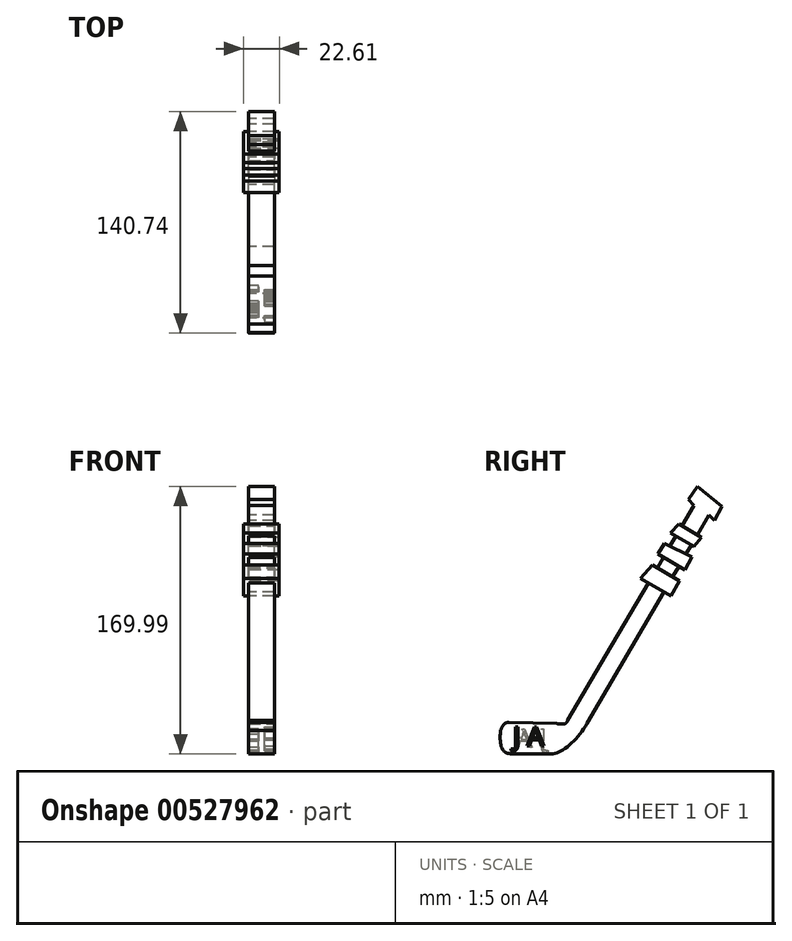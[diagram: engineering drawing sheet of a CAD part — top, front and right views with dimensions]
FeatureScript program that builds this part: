
annotation { "Feature Type Name" : "Feature", "Feature Type Description" : "" }
export const myFeature = defineFeature(function(context is Context, id is Id, definition is map)
    precondition{}
    {
        {
            var Q0;
            Q0=qCreatedBy(makeId("Right.planeOp"),FACE);
            var sketch = newSketch(context, id + "F0", { "sketchPlane" : qUnion([Q0])});
            skFitSpline(sketch, "E0", {"points": [v(0, 0) * mm, v(-16.58, -17.53) * mm, v(-30.01, -19.37) * mm], "startDerivative": vector(-21.4, -38.91) * mm, "endDerivative": vector(-38.92, 0.78) * mm});
            skLineSegment(sketch, "E1", {"start": v(-30.01, -19.37) * mm, "end": v(-45.64, -19.37) * mm});
            skFitSpline(sketch, "E2", {"points": [v(-45.64, -19.37) * mm, v(-53.94, -15.79) * mm, v(-54.85, -4.38) * mm, v(-54.85, -4.38) * mm], "startDerivative": vector(-22.65, 1.57) * mm, "endDerivative": vector(-0.12, 0.82) * mm});
            skFitSpline(sketch, "E3", {"points": [v(-54.85, -4.38) * mm, v(-52.18, 0) * mm, v(-49.35, 0.87) * mm], "startDerivative": vector(4.2, 9.27) * mm, "endDerivative": vector(6.95, 0.8) * mm});
            skLineSegment(sketch, "E4", {"start": v(-49.35, 0.87) * mm, "end": v(-18.89, 0) * mm});
            skFitSpline(sketch, "E5", {"points": [v(-18.89, 0) * mm, v(-13.68, 0) * mm, v(-12.19, 1.86) * mm, v(-11.32, 4.31) * mm], "startDerivative": vector(12.33, -3.5) * mm, "endDerivative": vector(-4.35, 0.33) * mm});
            skLineSegment(sketch, "E6", {"start": v(0, 0) * mm, "end": v(24.37, 41.62) * mm});
            skLineSegment(sketch, "E7", {"start": v(-12.19, 1.86) * mm, "end": v(12.19, 43.48) * mm});
            skPoint(sketch, "E7.endSnap0", {"position": v(12.19, 20.8) * mm});
            skLineSegment(sketch, "E8", {"start": v(12.19, 43.48) * mm, "end": v(37.33, 86.24) * mm});
            skLineSegment(sketch, "E9", {"start": v(24.37, 41.62) * mm, "end": v(50.5, 86.24) * mm});
            skLineSegment(sketch, "E10", {"start": v(37.33, 86.24) * mm, "end": v(68.12, 138.6) * mm});
            skLineSegment(sketch, "E11", {"start": v(50.5, 86.24) * mm, "end": v(77.56, 132.44) * mm});
            skLineSegment(sketch, "E12", {"start": v(77.56, 132.44) * mm, "end": v(81.23, 128.92) * mm});
            skLineSegment(sketch, "E13", {"start": v(68.12, 138.6) * mm, "end": v(64.66, 142.32) * mm});
            skLineSegment(sketch, "E14", {"start": v(64.66, 142.32) * mm, "end": v(70.25, 150.56) * mm});
            skLineSegment(sketch, "E15", {"start": v(81.23, 128.92) * mm, "end": v(85.72, 137.8) * mm});
            skLineSegment(sketch, "E16", {"start": v(70.25, 150.56) * mm, "end": v(85.72, 137.8) * mm});
            skSolve(sketch);
        }
        {
            var Q0;
            Q0=makeQuery(id+"F0.imprint","IMPRINT",FACE,{"disambiguationData":[TD([[makeQuery(id+"F0.imprint","IMPRINT",EDGE,{"derivedFrom":sQuery(id+"F0.wireOp",EDGE,"E0")}),-1.0]])]});
            extrude(context, id + "F1", {"entities" : qUnion([Q0]), "depth" : 16.5 * mm, "offsetDistance" : 25.4 * mm});
        }
        {
            var Q0;
            Q0=makeQuery(id+"F1.opExtrude","CAP_FACE",FACE,{"disambiguationData":[OSD([sQuery(id+"F0.wireOp",EDGE,"E0"),sQuery(id+"F0.wireOp",EDGE,"E1"),sQuery(id+"F0.wireOp",EDGE,"E2"),sQuery(id+"F0.wireOp",EDGE,"E3"),sQuery(id+"F0.wireOp",EDGE,"E4"),sQuery(id+"F0.wireOp",EDGE,"E5"),sQuery(id+"F0.wireOp",EDGE,"E6"),sQuery(id+"F0.wireOp",EDGE,"E7"),sQuery(id+"F0.wireOp",EDGE,"E8"),sQuery(id+"F0.wireOp",EDGE,"E9"),sQuery(id+"F0.wireOp",EDGE,"E10"),sQuery(id+"F0.wireOp",EDGE,"E11"),sQuery(id+"F0.wireOp",EDGE,"E12"),sQuery(id+"F0.wireOp",EDGE,"E13"),sQuery(id+"F0.wireOp",EDGE,"E14"),sQuery(id+"F0.wireOp",EDGE,"E15"),sQuery(id+"F0.wireOp",EDGE,"E16")])],"isStart":false});
            var sketch = newSketch(context, id + "F2", { "sketchPlane" : qUnion([Q0])});
            skLineSegment(sketch, "E17", {"start": v(58.5, 126.73) * mm, "end": v(72.93, 118.24) * mm});
            skLineSegment(sketch, "E18", {"start": v(72.93, 118.24) * mm, "end": v(68.12, 112.37) * mm});
            skLineSegment(sketch, "E19", {"start": v(68.12, 112.37) * mm, "end": v(53.12, 121.19) * mm});
            skLineSegment(sketch, "E20", {"start": v(53.12, 121.19) * mm, "end": v(58.5, 126.73) * mm});
            skSolve(sketch);
        }
        {
            var Q0;
            {var subQ0=sQuery(id+"F2.wireOp",EDGE,"E20");Q0=makeQuery(id+"F2.imprint","IMPRINT",FACE,{"disambiguationData":[TD([[makeQuery(id+"F2.imprint","IMPRINT",EDGE,{"derivedFrom":subQ0}),-1.0]])]});}
            var Q1;
            {var subQ0=sQuery(id+"F2.wireOp",EDGE,"E17");var subQ1=makeQuery(id+"F1.opExtrude","CAP_EDGE",EDGE,{"disambiguationData":[OSD([sQuery(id+"F0.wireOp",EDGE,"E8"),sQuery(id+"F0.wireOp",EDGE,"E10")])],"isStart":false});var subQ2=makeQuery(id+"F2.imprint","INTERSECT",VERTEX,{"derivedFrom":[subQ1,subQ0]});Q1=makeQuery(id+"F2.imprint","IMPRINT",FACE,{"disambiguationData":[TD([[makeQuery(id+"F2.imprint","IMPRINT",EDGE,{"disambiguationData":[TD([[subQ2,-1.0]])],"derivedFrom":subQ0}),-1.0]])]});}
            var Q2;
            {var subQ0=sQuery(id+"F2.wireOp",EDGE,"E18");Q2=makeQuery(id+"F2.imprint","IMPRINT",FACE,{"disambiguationData":[TD([[makeQuery(id+"F2.imprint","IMPRINT",EDGE,{"derivedFrom":subQ0}),-1.0]])]});}
            extrude(context, id + "F3", {"entities" : qUnion([Q0, Q1, Q2]), "operationType" : NewBodyOperationType.ADD, "depth" : 3.05 * mm, "offsetDistance" : 25.4 * mm});
        }
        {
            var Q0;
            Q0 = qSketchRegion(id + "F2", true);
            extrude(context, id + "F4", {"entities" : qUnion([Q0]), "operationType" : NewBodyOperationType.ADD, "oppositeDirection" : true, "depth" : 19.56 * mm, "offsetDistance" : 25.4 * mm});
        }
        {
            var Q0;
            {var subQ1=sQuery(id+"F0.wireOp",EDGE,"E3");var subQ2=sQuery(id+"F0.wireOp",EDGE,"E10");var subQ3=sQuery(id+"F0.wireOp",EDGE,"E8");var subQ4=sQuery(id+"F0.wireOp",EDGE,"E7");var subQ5=sQuery(id+"F0.wireOp",EDGE,"E11");var subQ6=sQuery(id+"F0.wireOp",EDGE,"E9");var subQ7=sQuery(id+"F0.wireOp",EDGE,"E6");var subQ8=sQuery(id+"F0.wireOp",EDGE,"E5");var subQ9=sQuery(id+"F0.wireOp",EDGE,"E4");var subQ10=sQuery(id+"F0.wireOp",EDGE,"E0");var subQ11=sQuery(id+"F0.wireOp",EDGE,"E1");var subQ12=sQuery(id+"F0.wireOp",EDGE,"E2");Q0=makeQuery(id+"F3.boolean.opBoolean","SPLIT",FACE,{"disambiguationData":[TD([makeQuery(id+"F1.opExtrude","SWEPT_FACE",FACE,{"disambiguationData":[OSD([subQ10])]})])],"derivedFrom":makeQuery(id+"F1.opExtrude","CAP_FACE",FACE,{"disambiguationData":[OSD([subQ10,subQ11,subQ12,subQ1,subQ9,subQ8,subQ7,subQ4,subQ3,subQ6,subQ2,subQ5,sQuery(id+"F0.wireOp",EDGE,"E12"),sQuery(id+"F0.wireOp",EDGE,"E13"),sQuery(id+"F0.wireOp",EDGE,"E14"),sQuery(id+"F0.wireOp",EDGE,"E15"),sQuery(id+"F0.wireOp",EDGE,"E16")])],"isStart":false})});}
            var sketch = newSketch(context, id + "F5", { "sketchPlane" : qUnion([Q0])});
            skLineSegment(sketch, "E21", {"start": v(49.34, 114.45) * mm, "end": v(45.32, 107.6) * mm});
            skLineSegment(sketch, "E22", {"start": v(45.32, 107.6) * mm, "end": v(62.17, 97.7) * mm});
            skLineSegment(sketch, "E23", {"start": v(62.17, 97.7) * mm, "end": v(66.91, 105.76) * mm});
            skLineSegment(sketch, "E24", {"start": v(66.91, 105.76) * mm, "end": v(49.34, 114.45) * mm});
            skSolve(sketch);
        }
        {
            var Q0;
            Q0 = qSketchRegion(id + "F5", true);
            extrude(context, id + "F6", {"entities" : qUnion([Q0]), "operationType" : NewBodyOperationType.ADD, "depth" : 3.05 * mm, "offsetDistance" : 25.4 * mm});
        }
        {
            var Q0;
            Q0 = qSketchRegion(id + "F5", true);
            extrude(context, id + "F7", {"entities" : qUnion([Q0]), "operationType" : NewBodyOperationType.ADD, "oppositeDirection" : true, "depth" : 19.56 * mm, "offsetDistance" : 25.4 * mm});
        }
        {
            var Q0;
            {var subQ0=sQuery(id+"F0.wireOp",EDGE,"E10");var subQ1=sQuery(id+"F0.wireOp",EDGE,"E8");var subQ3=sQuery(id+"F0.wireOp",EDGE,"E7");var subQ5=sQuery(id+"F0.wireOp",EDGE,"E11");var subQ6=sQuery(id+"F0.wireOp",EDGE,"E9");var subQ7=sQuery(id+"F0.wireOp",EDGE,"E6");var subQ9=sQuery(id+"F0.wireOp",EDGE,"E5");var subQ11=sQuery(id+"F0.wireOp",EDGE,"E4");var subQ13=sQuery(id+"F0.wireOp",EDGE,"E0");var subQ14=makeQuery(id+"F1.opExtrude","SWEPT_FACE",FACE,{"disambiguationData":[OSD([subQ13])]});var subQ15=sQuery(id+"F0.wireOp",EDGE,"E3");var subQ17=sQuery(id+"F0.wireOp",EDGE,"E1");var subQ20=sQuery(id+"F0.wireOp",EDGE,"E2");Q0=makeQuery(id+"F6.boolean.opBoolean","SPLIT",FACE,{"disambiguationData":[TD([subQ14])],"derivedFrom":makeQuery(id+"F3.boolean.opBoolean","SPLIT",FACE,{"disambiguationData":[TD([subQ14])],"derivedFrom":makeQuery(id+"F1.opExtrude","CAP_FACE",FACE,{"disambiguationData":[OSD([subQ13,subQ17,subQ20,subQ15,subQ11,subQ9,subQ7,subQ3,subQ1,subQ6,subQ0,subQ5,sQuery(id+"F0.wireOp",EDGE,"E12"),sQuery(id+"F0.wireOp",EDGE,"E13"),sQuery(id+"F0.wireOp",EDGE,"E14"),sQuery(id+"F0.wireOp",EDGE,"E15"),sQuery(id+"F0.wireOp",EDGE,"E16")])],"isStart":false})})});}
            var sketch = newSketch(context, id + "F8", { "sketchPlane" : qUnion([Q0])});
            skLineSegment(sketch, "E25", {"start": v(41.6, 100.64) * mm, "end": v(58.94, 90.44) * mm});
            skLineSegment(sketch, "E26", {"start": v(58.94, 90.44) * mm, "end": v(53.35, 80.94) * mm});
            skLineSegment(sketch, "E27", {"start": v(53.35, 80.94) * mm, "end": v(34.14, 92.24) * mm});
            skLineSegment(sketch, "E28", {"start": v(34.14, 92.24) * mm, "end": v(41.6, 100.64) * mm});
            skSolve(sketch);
        }
        {
            var Q0;
            Q0 = qSketchRegion(id + "F8", true);
            extrude(context, id + "F9", {"entities" : qUnion([Q0]), "operationType" : NewBodyOperationType.ADD, "depth" : 3.05 * mm, "offsetDistance" : 25.4 * mm});
        }
        {
            var Q0;
            Q0 = qSketchRegion(id + "F8", true);
            extrude(context, id + "F10", {"entities" : qUnion([Q0]), "operationType" : NewBodyOperationType.ADD, "oppositeDirection" : true, "depth" : 19.56 * mm, "offsetDistance" : 25.4 * mm});
        }
        {
            var Q0;
            {var subQ0=sQuery(id+"F0.wireOp",EDGE,"E10");var subQ1=sQuery(id+"F0.wireOp",EDGE,"E8");var subQ3=sQuery(id+"F0.wireOp",EDGE,"E7");var subQ5=sQuery(id+"F0.wireOp",EDGE,"E11");var subQ6=sQuery(id+"F0.wireOp",EDGE,"E9");var subQ7=sQuery(id+"F0.wireOp",EDGE,"E6");var subQ9=sQuery(id+"F0.wireOp",EDGE,"E5");var subQ12=sQuery(id+"F0.wireOp",EDGE,"E4");var subQ14=sQuery(id+"F0.wireOp",EDGE,"E0");var subQ15=makeQuery(id+"F1.opExtrude","SWEPT_FACE",FACE,{"disambiguationData":[OSD([subQ14])]});var subQ16=sQuery(id+"F0.wireOp",EDGE,"E3");var subQ18=sQuery(id+"F0.wireOp",EDGE,"E1");var subQ20=sQuery(id+"F0.wireOp",EDGE,"E2");Q0=makeQuery(id+"F9.boolean.opBoolean","SPLIT",FACE,{"disambiguationData":[TD([subQ15])],"derivedFrom":makeQuery(id+"F6.boolean.opBoolean","SPLIT",FACE,{"disambiguationData":[TD([subQ15])],"derivedFrom":makeQuery(id+"F3.boolean.opBoolean","SPLIT",FACE,{"disambiguationData":[TD([subQ15])],"derivedFrom":makeQuery(id+"F1.opExtrude","CAP_FACE",FACE,{"disambiguationData":[OSD([subQ14,subQ18,subQ20,subQ16,subQ12,subQ9,subQ7,subQ3,subQ1,subQ6,subQ0,subQ5,sQuery(id+"F0.wireOp",EDGE,"E12"),sQuery(id+"F0.wireOp",EDGE,"E13"),sQuery(id+"F0.wireOp",EDGE,"E14"),sQuery(id+"F0.wireOp",EDGE,"E15"),sQuery(id+"F0.wireOp",EDGE,"E16")])],"isStart":false})})})});}
            var sketch = newSketch(context, id + "F11", { "sketchPlane" : qUnion([Q0])});
            skText(sketch, "E29", { "text": "J A", "fontName": "OpenSans-Regular.ttf"});
            const initialGuessF11  = {"E29": [-0.0468, -0.01422, 1, 0, 0.01214]};
            skSetInitialGuess(sketch, initialGuessF11);
            skSolve(sketch);
        }
        {
            var Q0;
            Q0 = qSketchRegion(id + "F11", true);
            extrude(context, id + "F12", {"entities" : qUnion([Q0]), "operationType" : NewBodyOperationType.REMOVE, "oppositeDirection" : true, "depth" : 12.7 * mm, "offsetDistance" : 25.4 * mm, "symmetric" : true});
        }
        {
            var Q0;
            {var subQ0=sQuery(id+"F0.wireOp",EDGE,"E10");var subQ1=sQuery(id+"F0.wireOp",EDGE,"E8");var subQ4=sQuery(id+"F0.wireOp",EDGE,"E7");var subQ6=sQuery(id+"F0.wireOp",EDGE,"E11");var subQ7=sQuery(id+"F0.wireOp",EDGE,"E9");var subQ8=sQuery(id+"F0.wireOp",EDGE,"E6");var subQ10=sQuery(id+"F0.wireOp",EDGE,"E5");var subQ12=sQuery(id+"F0.wireOp",EDGE,"E4");var subQ14=sQuery(id+"F0.wireOp",EDGE,"E0");var subQ15=makeQuery(id+"F1.opExtrude","SWEPT_FACE",FACE,{"disambiguationData":[OSD([subQ14])]});var subQ16=sQuery(id+"F0.wireOp",EDGE,"E3");var subQ18=sQuery(id+"F0.wireOp",EDGE,"E1");var subQ20=sQuery(id+"F0.wireOp",EDGE,"E2");Q0=makeQuery(id+"F10.boolean.opBoolean","SPLIT",FACE,{"disambiguationData":[TD([subQ15])],"derivedFrom":makeQuery(id+"F7.boolean.opBoolean","SPLIT",FACE,{"disambiguationData":[TD([subQ15])],"derivedFrom":makeQuery(id+"F4.boolean.opBoolean","SPLIT",FACE,{"disambiguationData":[TD([subQ15])],"derivedFrom":makeQuery(id+"F1.opExtrude","CAP_FACE",FACE,{"disambiguationData":[OSD([subQ14,subQ18,subQ20,subQ16,subQ12,subQ10,subQ8,subQ4,subQ1,subQ7,subQ0,subQ6,sQuery(id+"F0.wireOp",EDGE,"E12"),sQuery(id+"F0.wireOp",EDGE,"E13"),sQuery(id+"F0.wireOp",EDGE,"E14"),sQuery(id+"F0.wireOp",EDGE,"E15"),sQuery(id+"F0.wireOp",EDGE,"E16")])],"isStart":true})})})});}
            var sketch = newSketch(context, id + "F13", { "sketchPlane" : qUnion([Q0])});
            skText(sketch, "E30", { "text": "J A", "fontName": "OpenSans-Regular.ttf"});
            const initialGuessF13  = {"E30": [0.02604, -0.0152, 1, 0, 0.01192]};
            skSetInitialGuess(sketch, initialGuessF13);
            skSolve(sketch);
        }
        {
            var Q0;
            Q0 = qSketchRegion(id + "F13", true);
            extrude(context, id + "F14", {"entities" : qUnion([Q0]), "operationType" : NewBodyOperationType.REMOVE, "oppositeDirection" : true, "depth" : 12.7 * mm, "offsetDistance" : 25.4 * mm, "symmetric" : true});
        }
    });
